# Revit family: DLB060015
name_source: partatom
category: Appareils sanitaires
revit_build: Autodesk Revit 2015 (Build: 20140606_1530(x64)
units: mm (PartAtom-declared; Revit-internal decimal feet)

## types (1)
- Type 1
    Category = Urinal
    Commentaires du type = Wall-hung single urinal
    Description = French manufacturer Delabie is a leader in the European sanitary ware market for non-domestic places. Water controls, solutions for disabled people, sanitary ware, for schools, leisure centres, offices, hospitals, airports…
    Fabricant = DELABIE
    Features  = Wall-hung single bowl urinal.
Compatible with all standard frame systems on the market.
Bacteriostatic 304 stainless steel. Stainless steel thickness: 1.2mm.
Rear water inlet.
Recessed horizontal waste outlet.
Supplied with 1½" P trap, fixing elements and theft prevention TORX security screws.
CE marked. Complies with European standard EN 13407 for 2L flush.
Weight: 7.5kg.
    Finish = Polished satin
    Grade = CE
    ManufacturerName = DELABIE
    ManufacturerURL = http://www.delabie.com
    Material = 304 stainless steel
    ModelNumber = 134770
    Modèle = DELTA urinal
    Name = DELTA urinal
    NominalHeight = 585 mm  [stored 1.91929 ft]
    NominalLength = 350 mm  [stored 1.14829 ft]
    NominalWidth = 385 mm  [stored 1.26312 ft]
    ProductInformation = http://www.delabie.com
    Radius (In) = 19 mm  [stored 0.062336 ft]
    Radius (Out) = 42 mm
    SerialNumber = 3456330153720
    URL = http://www.delabie.com
    Version = v1
    WarrantyDescription = Any manufacturing defect
    WarrantyDurationUnit = 10 years
    Weight = 7.5kg

note: [stored X ft] marks values corroborated as IEEE doubles in the binary element streams (Revit-internal decimal feet)

## geometry (parser evidence)
native form markers: Blend x24, Sweep x11
no freeform markers — native parametric forms only
